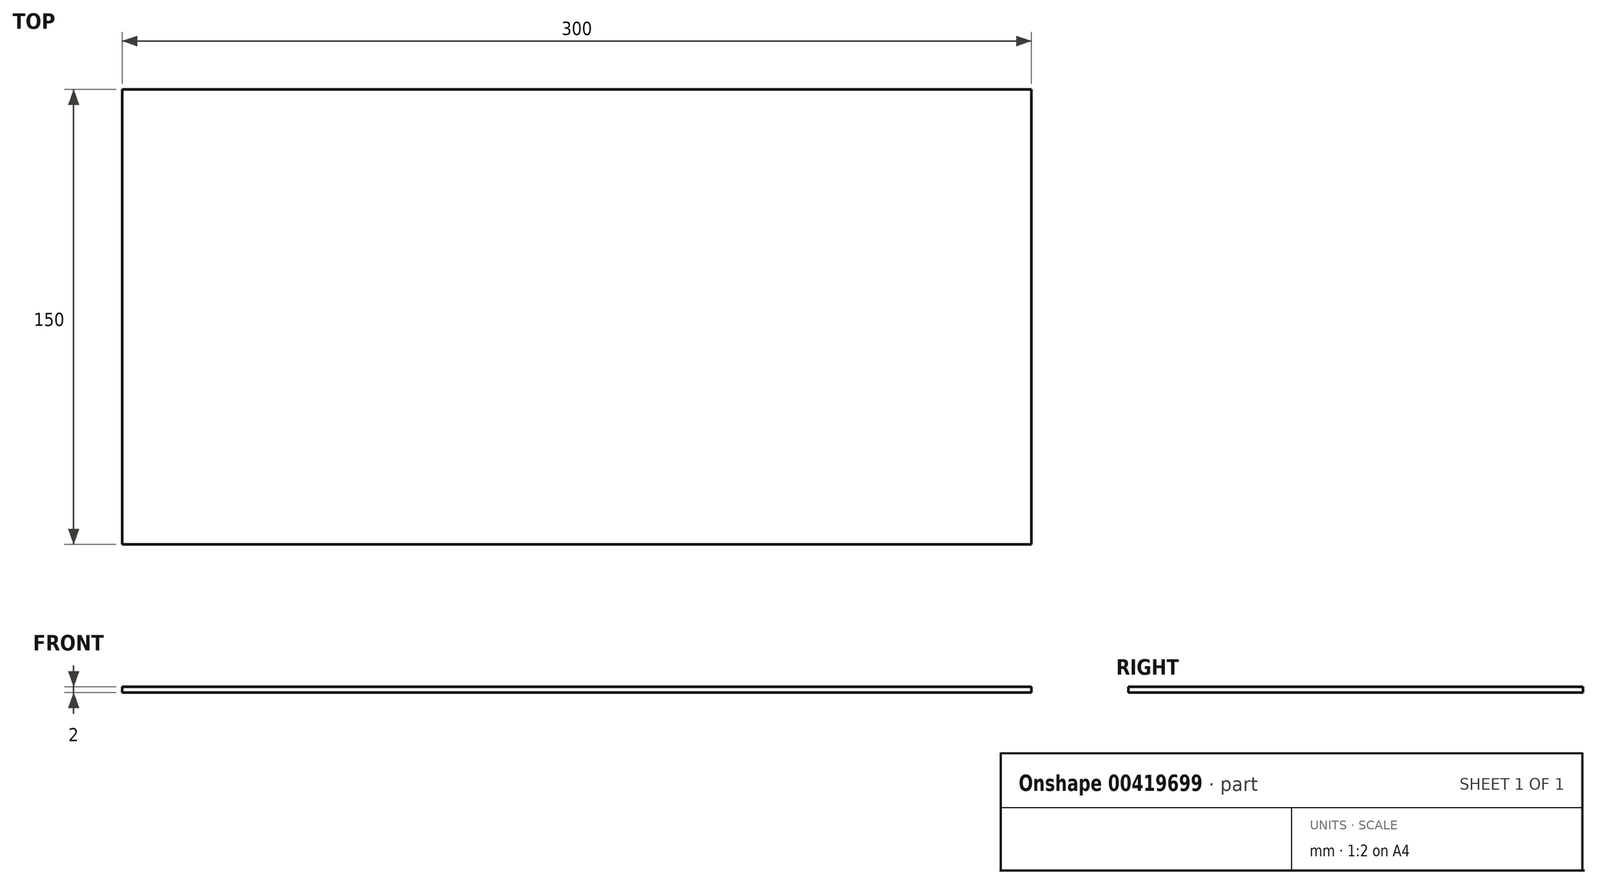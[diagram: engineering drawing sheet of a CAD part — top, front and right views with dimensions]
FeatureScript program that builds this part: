
annotation { "Feature Type Name" : "Feature", "Feature Type Description" : "" }
export const myFeature = defineFeature(function(context is Context, id is Id, definition is map)
    precondition{}
    {
        {
            var Q0;
            Q0=qCreatedBy(makeId("Top.planeOp"),FACE);
            var sketch = newSketch(context, id + "F0", { "sketchPlane" : qUnion([Q0])});
            skLineSegment(sketch, "E0.bottom", {"start": v(-150, 75) * mm, "end": v(150, 75) * mm});
            skLineSegment(sketch, "E0.top", {"start": v(-150, -75) * mm, "end": v(150, -75) * mm});
            skLineSegment(sketch, "E0.left", {"start": v(-150, 75) * mm, "end": v(-150, -75) * mm});
            skLineSegment(sketch, "E0.right", {"start": v(150, 75) * mm, "end": v(150, -75) * mm});
            skSolve(sketch);
        }
        {
            var Q0;
            Q0=makeQuery(id+"F0.imprint","IMPRINT",FACE,{"disambiguationData":[TD([[makeQuery(id+"F0.imprint","IMPRINT",EDGE,{"derivedFrom":sQuery(id+"F0.wireOp",EDGE,"E0.bottom")}),-1.0]])]});
            extrude(context, id + "F1", {"entities" : qUnion([Q0]), "depth" : 2 * mm});
        }
    });
